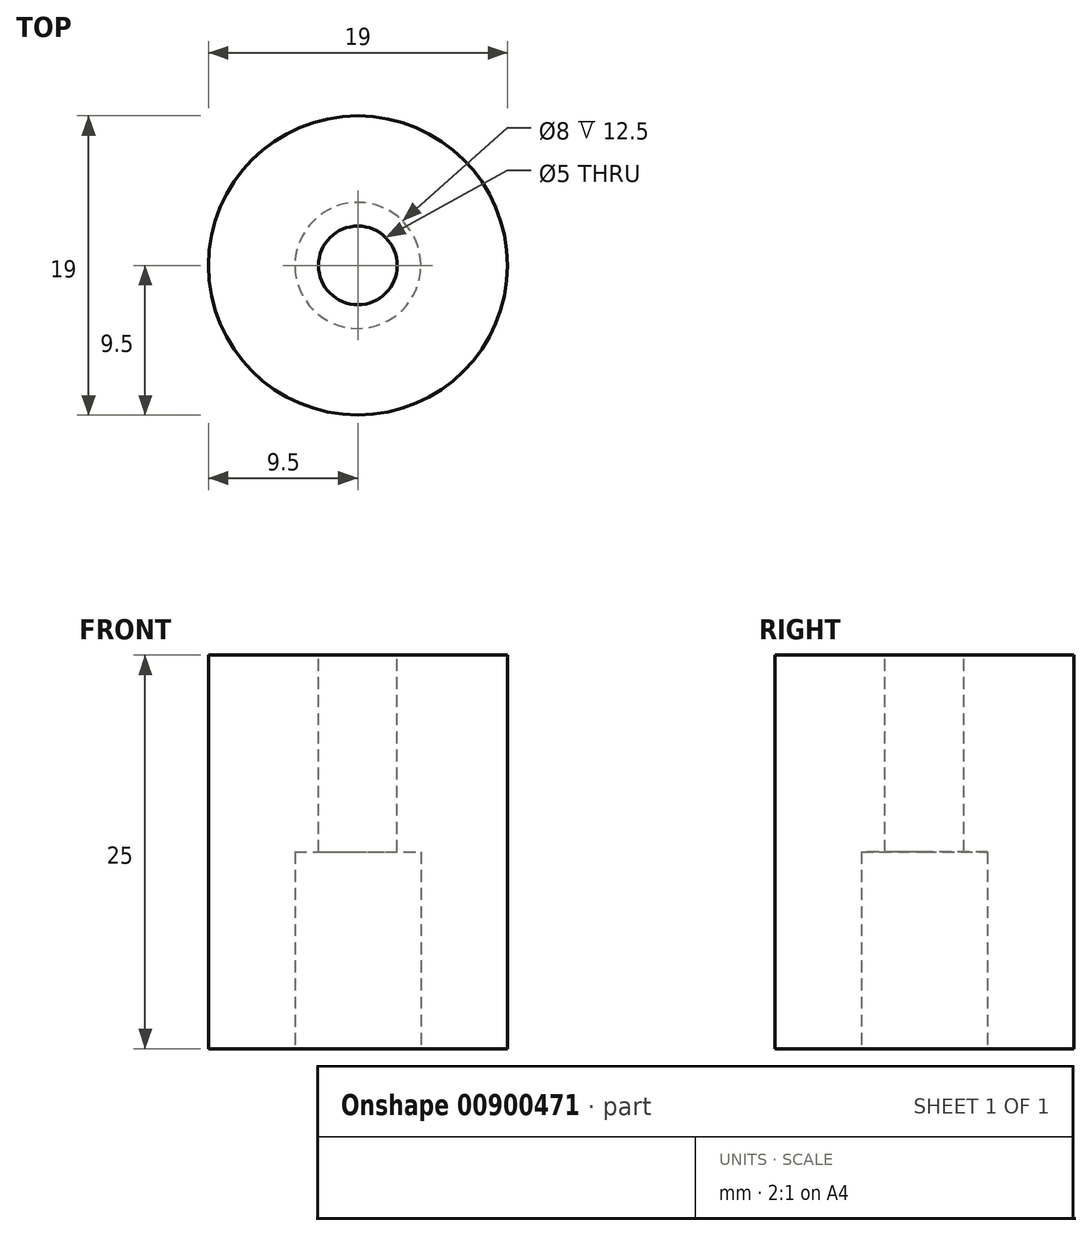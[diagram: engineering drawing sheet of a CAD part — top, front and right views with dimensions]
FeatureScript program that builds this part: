
annotation { "Feature Type Name" : "Feature", "Feature Type Description" : "" }
export const myFeature = defineFeature(function(context is Context, id is Id, definition is map)
    precondition{}
    {
        {
            var Q0;
            Q0=qCreatedBy(makeId("Top.planeOp"),FACE);
            var sketch = newSketch(context, id + "F0", { "sketchPlane" : qUnion([Q0])});
            skCircle(sketch, "E0", {"center": v(0, 0) * mm, "radius": 9.5 * mm});
            skSolve(sketch);
        }
        {
            var Q0;
            Q0=makeQuery(id+"F0.imprint","IMPRINT",FACE,{"disambiguationData":[TD([[makeQuery(id+"F0.imprint","IMPRINT",EDGE,{"derivedFrom":sQuery(id+"F0.wireOp",EDGE,"E0")}),1.0]])]});
            extrude(context, id + "F1", {"entities" : qUnion([Q0]), "depth" : 25 * mm, "offsetDistance" : 25 * mm});
        }
        {
            var Q0;
            Q0=makeQuery(id+"F1.opExtrude","CAP_FACE",FACE,{"disambiguationData":[OSD([sQuery(id+"F0.wireOp",EDGE,"E0")])],"isStart":true});
            var sketch = newSketch(context, id + "F2", { "sketchPlane" : qUnion([Q0])});
            skCircle(sketch, "E1", {"center": v(0, 0) * mm, "radius": 4 * mm});
            skSolve(sketch);
        }
        {
            var Q0;
            Q0=makeQuery(id+"F1.opExtrude","CAP_FACE",FACE,{"disambiguationData":[OSD([sQuery(id+"F0.wireOp",EDGE,"E0")])],"isStart":false});
            var sketch = newSketch(context, id + "F3", { "sketchPlane" : qUnion([Q0])});
            skCircle(sketch, "E2", {"center": v(0, 0) * mm, "radius": 2.5 * mm});
            skSolve(sketch);
        }
        {
            var Q0;
            Q0=makeQuery(id+"F2.imprint","IMPRINT",FACE,{"disambiguationData":[TD([[makeQuery(id+"F2.imprint","IMPRINT",EDGE,{"derivedFrom":sQuery(id+"F2.wireOp",EDGE,"E1")}),1.0]])]});
            extrude(context, id + "F4", {"entities" : qUnion([Q0]), "operationType" : NewBodyOperationType.REMOVE, "oppositeDirection" : true, "depth" : 12.5 * mm, "offsetDistance" : 25 * mm});
        }
        {
            var Q0;
            Q0=makeQuery(id+"F3.imprint","IMPRINT",FACE,{"disambiguationData":[TD([[makeQuery(id+"F3.imprint","IMPRINT",EDGE,{"derivedFrom":sQuery(id+"F3.wireOp",EDGE,"E2")}),1.0]])]});
            extrude(context, id + "F5", {"entities" : qUnion([Q0]), "operationType" : NewBodyOperationType.REMOVE, "endBound" : BoundingType.UP_TO_NEXT, "oppositeDirection" : true, "depth" : 25 * mm, "offsetDistance" : 25 * mm});
        }
    });
